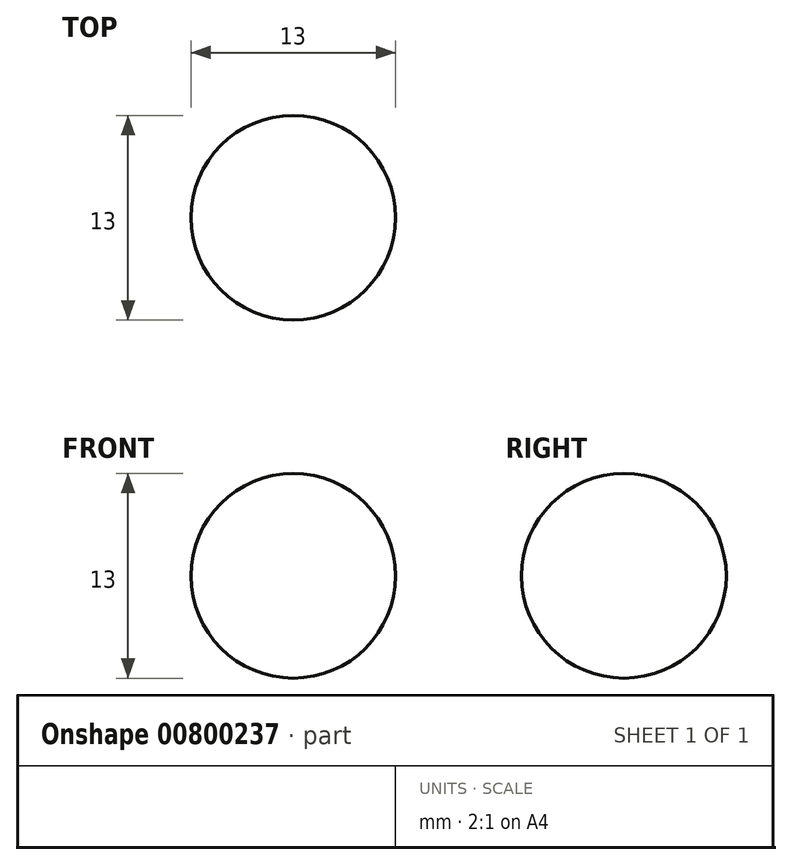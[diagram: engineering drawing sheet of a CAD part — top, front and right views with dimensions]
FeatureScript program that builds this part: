
annotation { "Feature Type Name" : "Feature", "Feature Type Description" : "" }
export const myFeature = defineFeature(function(context is Context, id is Id, definition is map)
    precondition{}
    {
        {
            var Q0;
            Q0=qCreatedBy(makeId("Front.planeOp"),FACE);
            var sketch = newSketch(context, id + "F0", { "sketchPlane" : qUnion([Q0])});
            skCircle(sketch, "E0", {"center": v(0, 0) * mm, "radius": 6.5 * mm});
            skLineSegment(sketch, "E1", {"start": v(0, 6.5) * mm, "end": v(0, -6.5) * mm});
            skSolve(sketch);
        }
        {
            var Q0;
            {var subQ0=sQuery(id+"F0.wireOp",EDGE,"E1");Q0=makeQuery(id+"F0.imprint","IMPRINT",FACE,{"disambiguationData":[TD([[makeQuery(id+"F0.imprint","IMPRINT",EDGE,{"derivedFrom":subQ0}),-1.0]])]});}
            var Q1;
            Q1=sQuery(id+"F0.wireOp",EDGE,"E1");
            revolve(context, id + "F1", {"surfaceOperationType" : NewSurfaceOperationType.NEW, "entities" : qUnion([Q0]), "axis" : qUnion([Q1]), "revolveType" : RevolveType.FULL});
        }
    });
